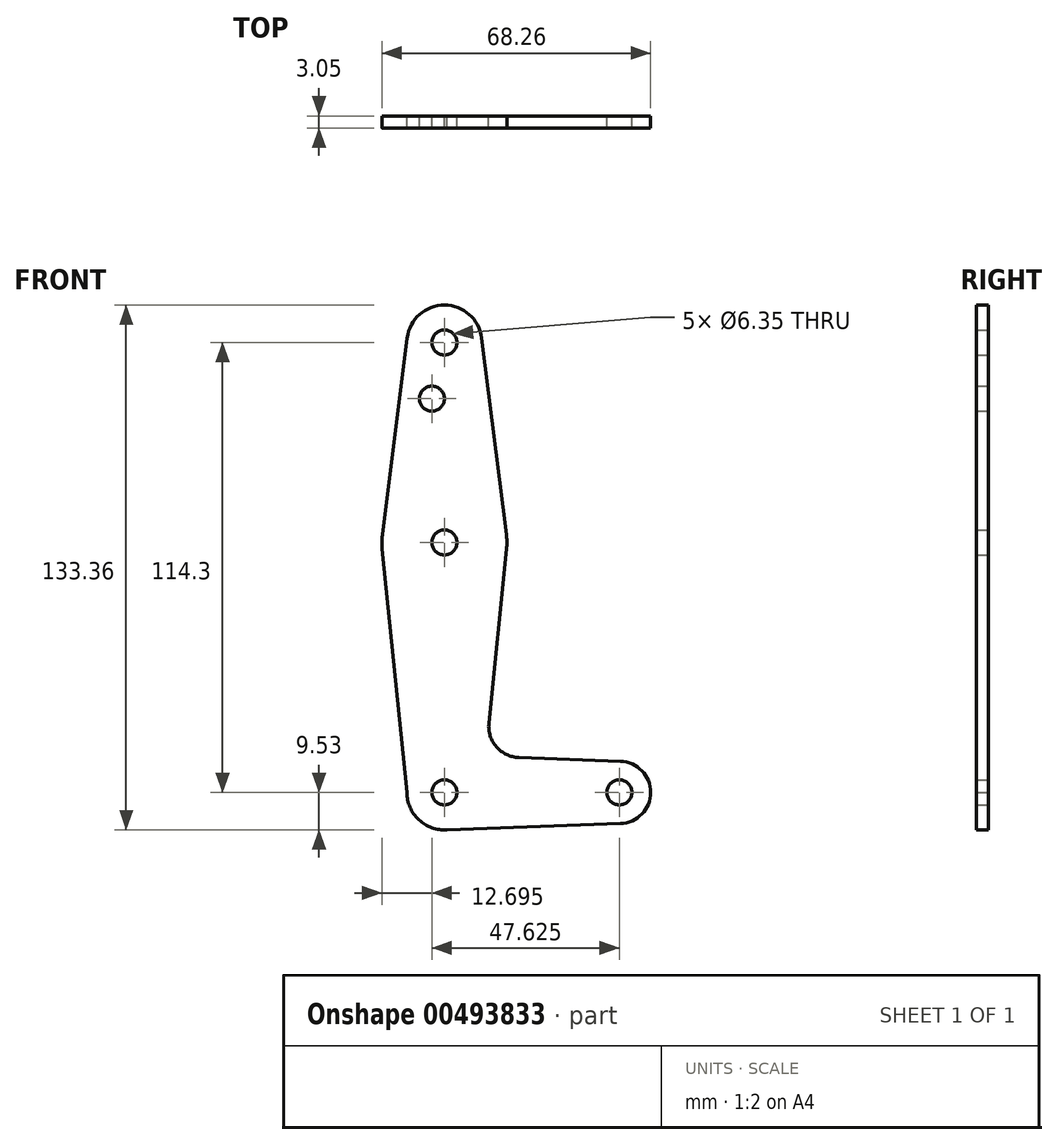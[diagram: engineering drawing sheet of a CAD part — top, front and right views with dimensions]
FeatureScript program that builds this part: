
annotation { "Feature Type Name" : "Feature", "Feature Type Description" : "" }
export const myFeature = defineFeature(function(context is Context, id is Id, definition is map)
    precondition{}
    {
        {
            var Q0;
            Q0=qCreatedBy(makeId("Front.planeOp"),FACE);
            var sketch = newSketch(context, id + "F0", { "sketchPlane" : qUnion([Q0])});
            skLineSegment(sketch, "E0", {"start": v(0, 0) * mm, "end": v(0, 114.3) * mm, "construction": true});
            skLineSegment(sketch, "E1", {"start": v(0, 0) * mm, "end": v(44.45, 0) * mm, "construction": true});
            skCircle(sketch, "E2", {"center": v(0, 114.3) * mm, "radius": 9.53 * mm});
            skCircle(sketch, "E3", {"center": v(0, 63.5) * mm, "radius": 15.88 * mm});
            skCircle(sketch, "E4", {"center": v(0, 0) * mm, "radius": 9.53 * mm});
            skCircle(sketch, "E5", {"center": v(44.45, 0) * mm, "radius": 7.94 * mm});
            skLineSegment(sketch, "E6", {"start": v(-9.45, 115.5) * mm, "end": v(-15.75, 65.48) * mm});
            skLineSegment(sketch, "E7", {"start": v(-9.53, 0) * mm, "end": v(-15.8, 61.9) * mm});
            skLineSegment(sketch, "E8", {"start": v(9.45, 115.5) * mm, "end": v(15.75, 65.48) * mm});
            skLineSegment(sketch, "E9", {"start": v(11.3, 17.6) * mm, "end": v(15.8, 61.9) * mm});
            skLineSegment(sketch, "E10", {"start": v(18.93, 8.85) * mm, "end": v(44.73, 7.93) * mm});
            skLineSegment(sketch, "E11", {"start": v(0, -9.53) * mm, "end": v(44.73, -7.93) * mm});
            skCircle(sketch, "E12", {"center": v(0, 114.3) * mm, "radius": 3.18 * mm});
            skCircle(sketch, "E13", {"center": v(0, 63.5) * mm, "radius": 3.18 * mm});
            skCircle(sketch, "E14", {"center": v(0, 0) * mm, "radius": 3.18 * mm});
            skCircle(sketch, "E15", {"center": v(44.45, 0) * mm, "radius": 3.18 * mm});
            skArc(sketch, "E16.filletArc", {"start": v(11.3, 17.6) * mm, "mid": v(13.22, 11.57) * mm, "end": v(18.93, 8.85) * mm});
            skCircle(sketch, "E17", {"center": v(-3.18, 100.03) * mm, "radius": 3.18 * mm});
            skSolve(sketch);
        }
        {
            var Q0;
            Q0 = qSketchRegion(id + "F0", true);
            extrude(context, id + "F1", {"entities" : qUnion([Q0]), "depth" : 3.05 * mm});
        }
    });
